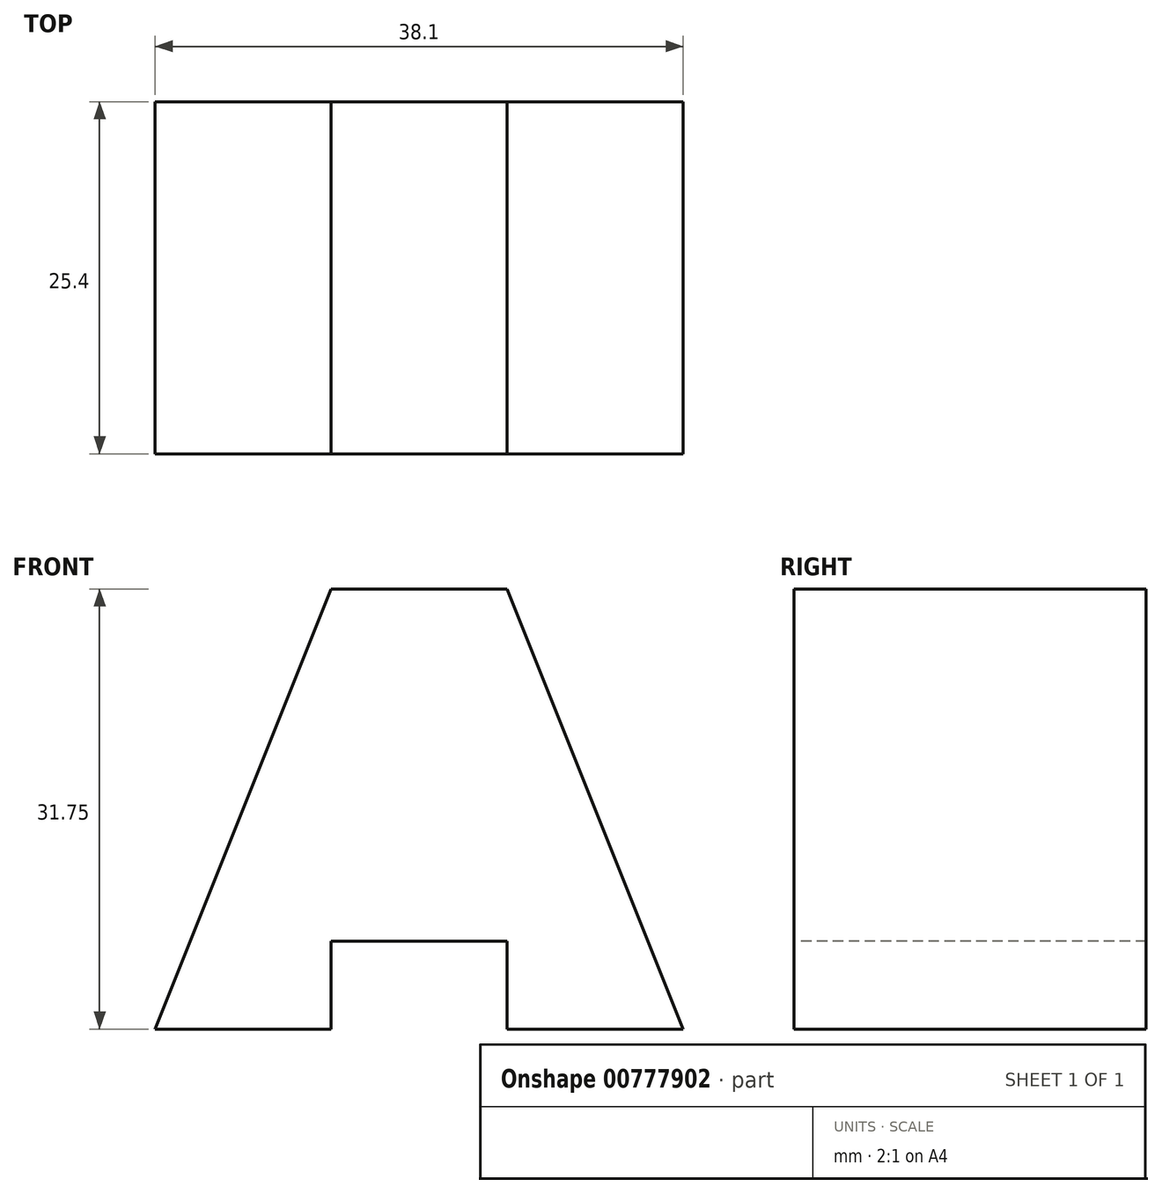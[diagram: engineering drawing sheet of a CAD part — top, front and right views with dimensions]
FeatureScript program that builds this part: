
annotation { "Feature Type Name" : "Feature", "Feature Type Description" : "" }
export const myFeature = defineFeature(function(context is Context, id is Id, definition is map)
    precondition{}
    {
        {
            var Q0;
            Q0=qCreatedBy(makeId("Front.planeOp"),FACE);
            var sketch = newSketch(context, id + "F0", { "sketchPlane" : qUnion([Q0])});
            skLineSegment(sketch, "E0", {"start": v(0, 0) * mm, "end": v(38.1, 0) * mm});
            skLineSegment(sketch, "E1", {"start": v(38.1, 0) * mm, "end": v(38.1, 31.75) * mm});
            skLineSegment(sketch, "E2", {"start": v(38.1, 31.75) * mm, "end": v(0, 31.75) * mm});
            skLineSegment(sketch, "E3", {"start": v(0, 31.75) * mm, "end": v(0, 0) * mm});
            skSolve(sketch);
        }
        {
            var Q0;
            Q0=makeQuery(id+"F0.imprint","IMPRINT",FACE,{"disambiguationData":[TD([[makeQuery(id+"F0.imprint","IMPRINT",EDGE,{"derivedFrom":sQuery(id+"F0.wireOp",EDGE,"E0")}),1.0]])]});
            extrude(context, id + "F1", {"entities" : qUnion([Q0]), "depth" : 25.4 * mm, "offsetDistance" : 25.4 * mm});
        }
        {
            var Q0;
            Q0=makeQuery(id+"F1.opExtrude","CAP_FACE",FACE,{"disambiguationData":[OSD([sQuery(id+"F0.wireOp",EDGE,"E0"),sQuery(id+"F0.wireOp",EDGE,"E1"),sQuery(id+"F0.wireOp",EDGE,"E2"),sQuery(id+"F0.wireOp",EDGE,"E3")])],"isStart":false});
            var sketch = newSketch(context, id + "F2", { "sketchPlane" : qUnion([Q0])});
            skLineSegment(sketch, "E4", {"start": v(0, 0) * mm, "end": v(12.7, 0) * mm});
            skLineSegment(sketch, "E5", {"start": v(38.1, 0) * mm, "end": v(25.4, 0) * mm});
            skLineSegment(sketch, "E6", {"start": v(25.4, 0) * mm, "end": v(25.4, 6.35) * mm});
            skLineSegment(sketch, "E7", {"start": v(12.7, 0) * mm, "end": v(12.7, 6.35) * mm});
            skLineSegment(sketch, "E8", {"start": v(12.7, 6.35) * mm, "end": v(25.4, 6.35) * mm});
            skSolve(sketch);
        }
        {
            var Q0;
            {var subQ0=sQuery(id+"F2.wireOp",EDGE,"E6");Q0=makeQuery(id+"F2.imprint","IMPRINT",FACE,{"disambiguationData":[TD([[makeQuery(id+"F2.imprint","IMPRINT",EDGE,{"derivedFrom":subQ0}),1.0]])]});}
            extrude(context, id + "F3", {"entities" : qUnion([Q0]), "operationType" : NewBodyOperationType.REMOVE, "oppositeDirection" : true, "depth" : 25.4 * mm, "offsetDistance" : 25.4 * mm});
        }
        {
            var Q0;
            Q0=makeQuery(id+"F1.opExtrude","CAP_FACE",FACE,{"disambiguationData":[OSD([sQuery(id+"F0.wireOp",EDGE,"E0"),sQuery(id+"F0.wireOp",EDGE,"E1"),sQuery(id+"F0.wireOp",EDGE,"E2"),sQuery(id+"F0.wireOp",EDGE,"E3")])],"isStart":false});
            var sketch = newSketch(context, id + "F4", { "sketchPlane" : qUnion([Q0])});
            skLineSegment(sketch, "E9", {"start": v(0, 31.75) * mm, "end": v(12.7, 31.75) * mm});
            skLineSegment(sketch, "E10", {"start": v(12.7, 31.75) * mm, "end": v(0, 0) * mm});
            skLineSegment(sketch, "E11", {"start": v(38.1, 31.75) * mm, "end": v(25.4, 31.75) * mm});
            skLineSegment(sketch, "E12", {"start": v(25.4, 31.75) * mm, "end": v(38.1, 0) * mm});
            skSolve(sketch);
        }
        {
            var Q0;
            Q0=makeQuery(id+"F4.imprint","IMPRINT",FACE,{"disambiguationData":[TD([[makeQuery(id+"F4.imprint","IMPRINT",EDGE,{"derivedFrom":sQuery(id+"F4.wireOp",EDGE,"E9")}),1.0]])]});
            var Q1;
            Q1=makeQuery(id+"F4.imprint","IMPRINT",FACE,{"disambiguationData":[TD([[makeQuery(id+"F4.imprint","IMPRINT",EDGE,{"derivedFrom":sQuery(id+"F4.wireOp",EDGE,"E11")}),1.0]])]});
            extrude(context, id + "F5", {"entities" : qUnion([Q0, Q1]), "operationType" : NewBodyOperationType.REMOVE, "oppositeDirection" : true, "depth" : 25.4 * mm, "offsetDistance" : 25.4 * mm});
        }
    });
